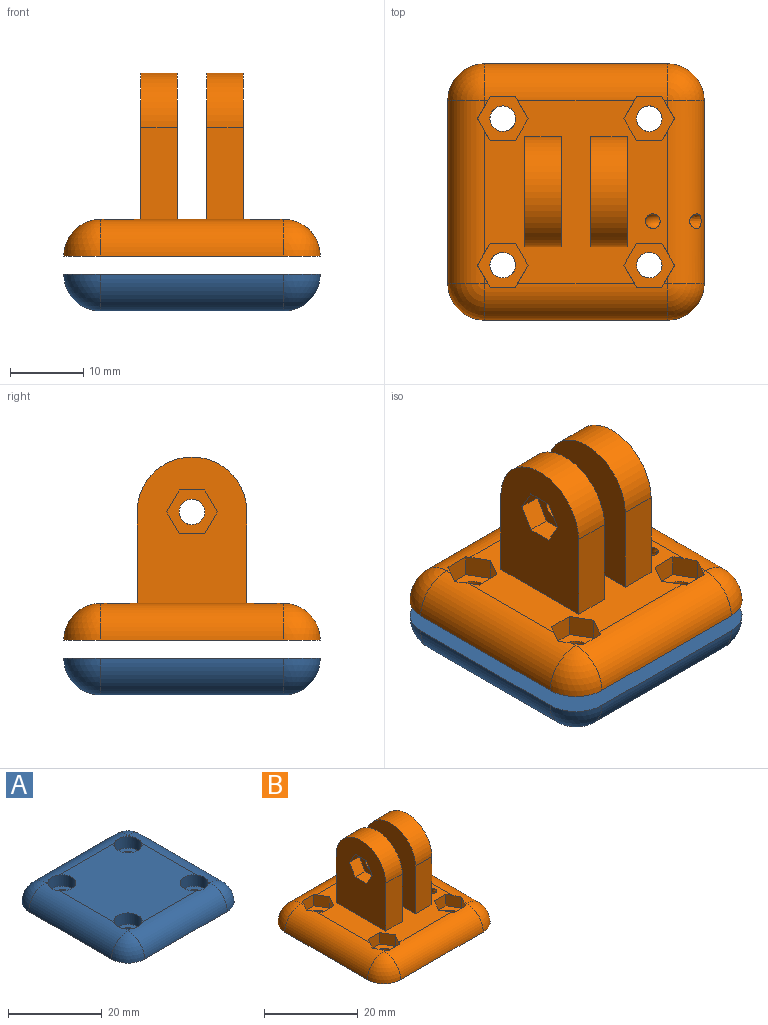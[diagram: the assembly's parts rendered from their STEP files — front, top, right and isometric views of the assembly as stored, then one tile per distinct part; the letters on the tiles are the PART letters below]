
ASSEMBLY  parts=2 mates=1
PART A: 26 faces, bbox 35x35x5 mm
  f0: plane 25x25mm, normal (0,0,1), area 519.7mm2, adj f10,f12,f14,f16,f19,f20,f23,f24
  f1: plane 0.84x0.84mm, normal (0,0,1), area 0.3mm2, adj f12,f19,f20
  f2: plane 0.84x0.84mm, normal (0,0,1), area 0.3mm2, adj f14,f20,f24
  f3: plane 0.84x0.84mm, normal (0,0,1), area 0.3mm2, adj f10,f19,f23
  f4: cylinder r=1.75mm len=3.5mm, axis (0,0,-1), area 22mm2, adj f9,f15
  f5: cylinder r=1.75mm len=3.5mm, axis (0,0,-1), area 22mm2, adj f9,f17
  f6: cylinder r=1.75mm len=3.5mm, axis (0,0,-1), area 22mm2, adj f9,f11
  f7: cylinder r=1.75mm len=3.5mm, axis (0,0,-1), area 22mm2, adj f9,f13
  f8: plane 0.84x0.84mm, normal (0,0,1), area 0.3mm2, adj f16,f23,f24
  f9: plane 35x35mm, normal (0,0,-1), area 1165.1mm2, adj f4,f5,f6,f7,f18,f19,f20,f21
  f10: cylinder r=3mm len=6mm, axis (0,0,1), area 56.5mm2, adj f0,f3,f11,f19,f23
  f11: plane 6x6mm, normal (0,0,1), area 18.7mm2, adj f6,f10
  f12: cylinder r=3mm len=6mm, axis (0,0,1), area 56.5mm2, adj f0,f1,f13,f19,f20
  f13: plane 6x6mm, normal (0,0,1), area 18.7mm2, adj f7,f12
  f14: cylinder r=3mm len=6mm, axis (0,0,1), area 56.5mm2, adj f0,f2,f15,f20,f24
  f15: plane 6x6mm, normal (0,0,1), area 18.7mm2, adj f4,f14
  f16: cylinder r=3mm len=6mm, axis (0,0,1), area 56.5mm2, adj f0,f8,f17,f23,f24
  f17: plane 6x6mm, normal (0,0,1), area 18.7mm2, adj f5,f16
  f18: sphere r=5mm, area 39.3mm2, adj f9,f19,f20
  f19: cylinder r=5mm len=25mm, axis (1,0,0), area 194.1mm2, adj f0,f1,f3,f9,f10,f12,f18,f21
  f20: cylinder r=5mm len=25mm, axis (0,-1,0), area 194.1mm2, adj f0,f1,f2,f9,f12,f14,f18,f22
  f21: sphere r=5mm, area 39.3mm2, adj f9,f19,f23
  f22: sphere r=5mm, area 39.3mm2, adj f9,f20,f24
  f23: cylinder r=5mm len=25mm, axis (0,1,0), area 194.1mm2, adj f0,f3,f8,f9,f10,f16,f21,f25
  f24: cylinder r=5mm len=25mm, axis (-1,0,0), area 194.1mm2, adj f0,f2,f8,f9,f14,f16,f22,f25
  f25: sphere r=5mm, area 39.3mm2, adj f9,f23,f24
PART B: 69 faces, bbox 39.6x35x25 mm
  f0: cylinder r=1.75mm len=3.5mm, axis (1,0,0), area 22mm2, adj f4,f66
  f1: cylinder r=1.75mm len=3.5mm, axis (1,0,0), area 22mm2, adj f2,f59
  f2: plane 20x15mm, normal (-1,0,0), area 266.2mm2, adj f1,f5,f7,f9,f57
  f3: plane 20x15mm, normal (1,0,0), area 247.6mm2, adj f5,f7,f9,f57,f58
  f4: plane 20x15mm, normal (1,0,0), area 266.2mm2, adj f0,f6,f8,f9,f56
  f5: plane 12.5x5mm, normal (0,1,0), area 62.5mm2, adj f2,f3,f9,f57
  f6: plane 12.5x5mm, normal (0,1,0), area 62.5mm2, adj f4,f9,f55,f56
  f7: plane 12.5x5mm, normal (0,-1,0), area 62.5mm2, adj f2,f3,f9,f57
  f8: plane 12.5x5mm, normal (0,-1,0), area 62.5mm2, adj f4,f9,f55,f56
  f9: plane 25x25mm, normal (0,0,1), area 360.3mm2, adj f2,f3,f4,f5,f6,f7,f8,f19
  f10: plane 0.83x0.48mm, normal (0,0,1), area 0.2mm2, adj f26,f48,f49
  f11: plane 0.83x0.48mm, normal (0,0,1), area 0.2mm2, adj f38,f49,f53
  f12: plane 0.83x0.48mm, normal (0,0,1), area 0.2mm2, adj f24,f48,f52
  f13: cylinder r=1.75mm len=3.5mm, axis (0,0,-1), area 22mm2, adj f18,f39
  f14: cylinder r=1.75mm len=3.5mm, axis (0,0,-1), area 22mm2, adj f18,f32
  f15: cylinder r=1.75mm len=3.5mm, axis (0,0,-1), area 22mm2, adj f18,f25
  f16: cylinder r=1.75mm len=3.5mm, axis (0,0,-1), area 22mm2, adj f18,f46
  f17: plane 0.83x0.48mm, normal (0,0,1), area 0.2mm2, adj f43,f52,f53
  f18: plane 35x35mm, normal (0,0,-1), area 1165.1mm2, adj f13,f14,f15,f16,f47,f48,f49,f50
  f19: plane 3.01x3.01mm, normal (0.87,0.5,0), area 10.3mm2, adj f9,f20,f24,f25,f52
  f20: plane 3.46x3mm, normal (0,1,0), area 10.4mm2, adj f9,f19,f21,f25
  f21: plane 3x3mm, normal (-0.87,0.5,0), area 10.4mm2, adj f9,f20,f22,f25
  f22: plane 3x3mm, normal (-0.87,-0.5,0), area 10.4mm2, adj f9,f21,f23,f25,f48
  f23: plane 3.46x2.98mm, normal (0,-1,0), area 10.3mm2, adj f22,f24,f25,f48
  f24: plane 3.01x3.01mm, normal (0.87,-0.5,0), area 10.3mm2, adj f12,f19,f23,f25,f48,f52
  f25: plane 6.93x6mm, normal (0,0,1), area 21.6mm2, adj f15,f19,f20,f21,f22,f23,f24
  f26: plane 3.01x3.01mm, normal (-0.87,-0.5,0), area 10.3mm2, adj f10,f27,f31,f32,f48,f49
  f27: plane 3.46x2.98mm, normal (0,-1,0), area 10.3mm2, adj f26,f28,f32,f48
  f28: plane 3x3mm, normal (0.87,-0.5,0), area 10.4mm2, adj f9,f27,f29,f32,f48
  f29: plane 3x3mm, normal (0.87,0.5,0), area 10.4mm2, adj f9,f28,f30,f32
  f30: plane 3.46x3mm, normal (0,1,0), area 10.4mm2, adj f9,f29,f31,f32
  f31: plane 3.01x3.01mm, normal (-0.87,0.5,0), area 10.3mm2, adj f9,f26,f30,f32,f49
  f32: plane 6.93x6mm, normal (0,0,1), area 21.6mm2, adj f14,f26,f27,f28,f29,f30,f31
  f33: plane 3.01x3.01mm, normal (-0.87,-0.5,0), area 10.3mm2, adj f9,f34,f38,f39,f49
  f34: plane 3.46x3mm, normal (0,-1,0), area 10.4mm2, adj f9,f33,f35,f39
  f35: plane 3x3mm, normal (0.87,-0.5,0), area 10.4mm2, adj f9,f34,f36,f39
  f36: plane 3x3mm, normal (0.87,0.5,0), area 10.4mm2, adj f9,f35,f37,f39,f53
  f37: plane 3.46x2.98mm, normal (0,1,0), area 10.3mm2, adj f36,f38,f39,f53
  f38: plane 3.01x3.01mm, normal (-0.87,0.5,0), area 10.3mm2, adj f11,f33,f37,f39,f49,f53
  f39: plane 6.93x6mm, normal (0,0,1), area 21.6mm2, adj f13,f33,f34,f35,f36,f37,f38
  f40: plane 3x3mm, normal (-0.87,-0.5,0), area 10.4mm2, adj f9,f41,f45,f46
  f41: plane 3.46x3mm, normal (0,-1,0), area 10.4mm2, adj f9,f40,f42,f46
  f42: plane 3.01x3.01mm, normal (0.87,-0.5,0), area 10.3mm2, adj f9,f41,f43,f46,f52
  f43: plane 3.01x3.01mm, normal (0.87,0.5,0), area 10.3mm2, adj f17,f42,f44,f46,f52,f53
  f44: plane 3.46x2.98mm, normal (0,1,0), area 10.3mm2, adj f43,f45,f46,f53
  f45: plane 3x3mm, normal (-0.87,0.5,0), area 10.4mm2, adj f9,f40,f44,f46,f53
  f46: plane 6.93x6mm, normal (0,0,1), area 21.6mm2, adj f16,f40,f41,f42,f43,f44,f45
  f47: sphere r=5mm, area 39.3mm2, adj f18,f48,f49
  f48: cylinder r=5mm len=25mm, axis (1,0,0), area 192.6mm2, adj f9,f10,f12,f18,f22,f23,f24,f26
  f49: cylinder r=5mm len=25mm, axis (0,-1,0), area 189.1mm2, adj f9,f10,f11,f18,f26,f31,f33,f38
  f50: sphere r=5mm, area 39.3mm2, adj f18,f48,f52
  f51: sphere r=5mm, area 39.3mm2, adj f18,f49,f53
  f52: cylinder r=5mm len=25mm, axis (0,1,0), area 193.1mm2, adj f9,f12,f17,f18,f19,f24,f42,f43
  f53: cylinder r=5mm len=25mm, axis (-1,0,0), area 192.6mm2, adj f9,f11,f17,f18,f36,f37,f38,f43
  f54: sphere r=5mm, area 39.3mm2, adj f18,f52,f53
  f55: plane 20x15mm, normal (-1,0,0), area 244.7mm2, adj f6,f8,f9,f56,f60,f61,f62,f63
  f56: cylinder r=7.5mm len=15mm, axis (1,0,0), area 117.8mm2, adj f4,f6,f8,f55
  f57: cylinder r=7.5mm len=15mm, axis (1,0,0), area 117.8mm2, adj f2,f3,f5,f7
  f58: cylinder r=3mm len=6mm, axis (1,0,0), area 56.5mm2, adj f3,f59
  f59: plane 6x6mm, normal (1,0,0), area 18.7mm2, adj f1,f58
  f60: plane 3x3mm, normal (0,0.87,-0.5), area 10.4mm2, adj f55,f61,f65,f66
  f61: plane 3.46x3mm, normal (0,0,-1), area 10.4mm2, adj f55,f60,f62,f66
  f62: plane 3x3mm, normal (0,-0.87,-0.5), area 10.4mm2, adj f55,f61,f63,f66
  f63: plane 3x3mm, normal (0,-0.87,0.5), area 10.4mm2, adj f55,f62,f64,f66
  f64: plane 3.46x3mm, normal (0,0,1), area 10.4mm2, adj f55,f63,f65,f66
  f65: plane 3x3mm, normal (0,0.87,0.5), area 10.4mm2, adj f55,f60,f64,f66
  f66: plane 6.93x6mm, normal (-1,0,0), area 21.6mm2, adj f0,f60,f61,f62,f63,f64,f65
  f67: torus R=2mm, axis (0,-1,0), area 19.6mm2, adj f9,f68
  f68: bspline ~9.66x4mm, area 24.7mm2, adj f49,f67
PLACE A rot(axis=(0.71,0.71,0),180deg) t=(0.99,-1.29,3.3)mm
PLACE B t=(0.99,-1.29,5.8)mm
MATE fastened A.f5 <-> B.f16  axis (0,0,1) through (8.49,6.21,3.3)mm
